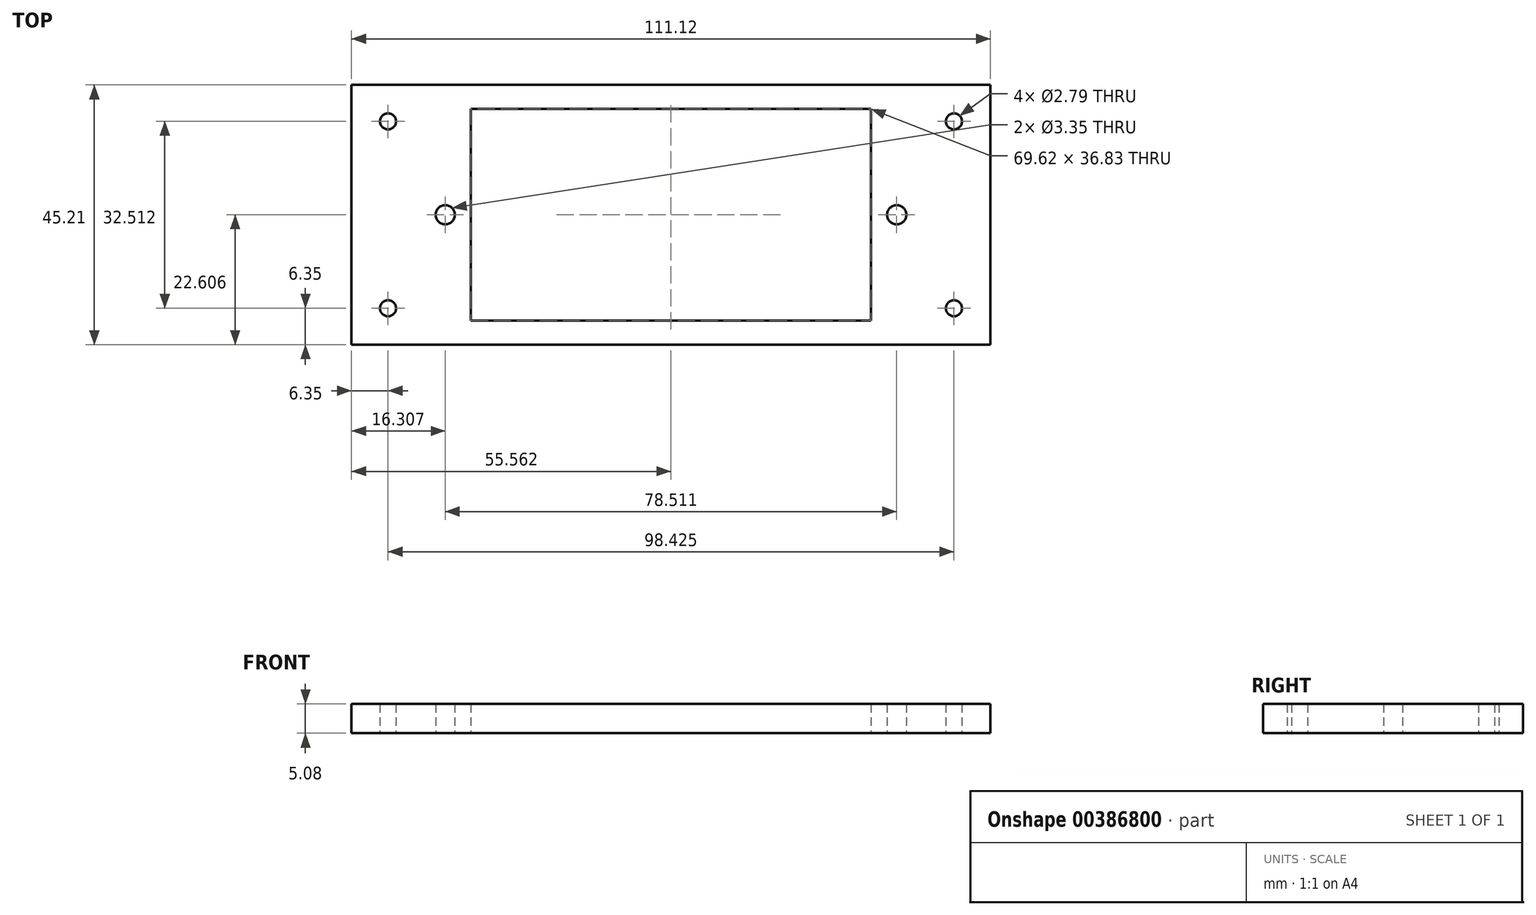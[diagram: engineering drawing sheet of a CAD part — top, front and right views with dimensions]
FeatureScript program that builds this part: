
annotation { "Feature Type Name" : "Feature", "Feature Type Description" : "" }
export const myFeature = defineFeature(function(context is Context, id is Id, definition is map)
    precondition{}
    {
        {
            var Q0;
            Q0=qCreatedBy(makeId("Top.planeOp"),FACE);
            var sketch = newSketch(context, id + "F0", { "sketchPlane" : qUnion([Q0])});
            skLineSegment(sketch, "E0.bottom", {"start": v(0, 0) * mm, "end": v(111.13, 0) * mm});
            skLineSegment(sketch, "E0.top", {"start": v(0, 45.21) * mm, "end": v(111.13, 45.21) * mm});
            skLineSegment(sketch, "E0.left", {"start": v(0, 0) * mm, "end": v(0, 45.21) * mm});
            skLineSegment(sketch, "E0.right", {"start": v(111.13, 0) * mm, "end": v(111.13, 45.21) * mm});
            skLineSegment(sketch, "E1", {"start": v(0, 38.86) * mm, "end": v(111.13, 38.86) * mm, "construction": true});
            skLineSegment(sketch, "E2", {"start": v(0, 6.35) * mm, "end": v(111.13, 6.35) * mm, "construction": true});
            skLineSegment(sketch, "E3", {"start": v(6.35, 45.21) * mm, "end": v(6.35, 0) * mm, "construction": true});
            skLineSegment(sketch, "E4", {"start": v(104.78, 45.21) * mm, "end": v(104.78, 0) * mm, "construction": true});
            skCircle(sketch, "E5", {"center": v(6.35, 38.86) * mm, "radius": 1.4 * mm});
            skCircle(sketch, "E6", {"center": v(6.35, 6.35) * mm, "radius": 1.4 * mm});
            skCircle(sketch, "E7", {"center": v(104.78, 38.86) * mm, "radius": 1.4 * mm});
            skCircle(sketch, "E8", {"center": v(104.78, 6.35) * mm, "radius": 1.4 * mm});
            skLineSegment(sketch, "E9", {"start": v(111.13, 41.02) * mm, "end": v(0, 41.02) * mm});
            skLineSegment(sketch, "E10", {"start": v(0, 4.2) * mm, "end": v(111.13, 4.2) * mm});
            skLineSegment(sketch, "E11", {"start": v(20.75, 45.21) * mm, "end": v(20.75, 0) * mm});
            skLineSegment(sketch, "E12", {"start": v(90.37, 45.21) * mm, "end": v(90.37, 0) * mm});
            skLineSegment(sketch, "E13", {"start": v(0, 22.6) * mm, "end": v(111.13, 22.6) * mm, "construction": true});
            skLineSegment(sketch, "E14", {"start": v(16.3, 45.21) * mm, "end": v(16.3, 0) * mm, "construction": true});
            skLineSegment(sketch, "E15", {"start": v(94.82, 45.21) * mm, "end": v(94.82, 0) * mm, "construction": true});
            skLineSegment(sketch, "E16", {"start": v(16.3, 0) * mm, "end": v(0, 0) * mm});
            skCircle(sketch, "E17", {"center": v(16.3, 22.6) * mm, "radius": 1.68 * mm});
            skCircle(sketch, "E18", {"center": v(94.82, 22.6) * mm, "radius": 1.68 * mm});
            skSolve(sketch);
        }
        {
            var Q0;
            Q0 = qSketchRegion(id + "F0", true);
            extrude(context, id + "F1", {"entities" : qUnion([Q0]), "depth" : 5.08 * mm});
        }
    });
